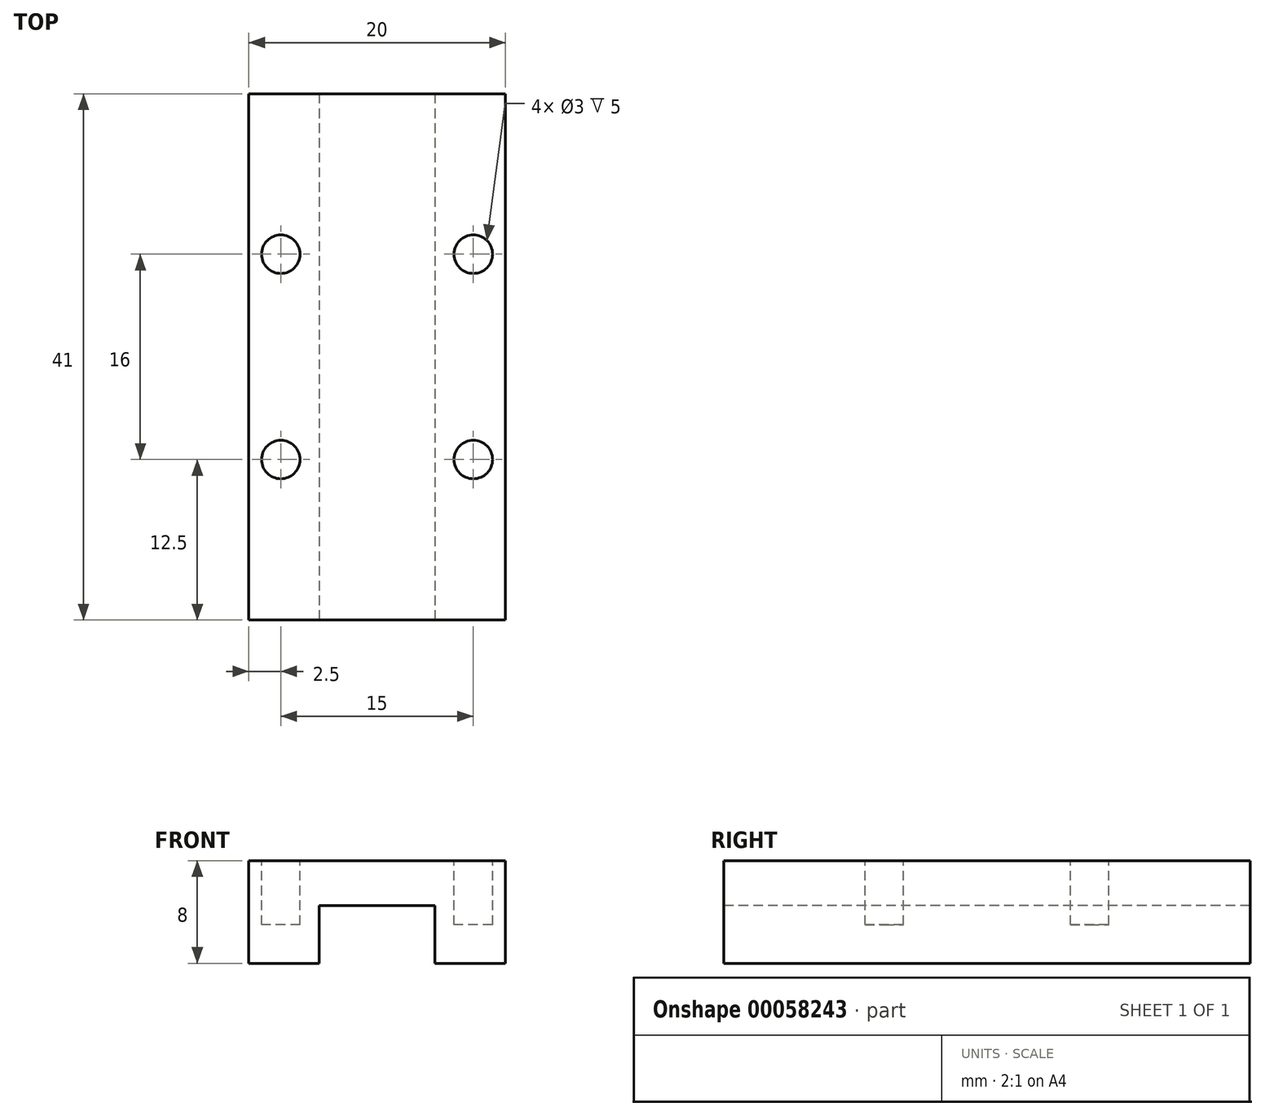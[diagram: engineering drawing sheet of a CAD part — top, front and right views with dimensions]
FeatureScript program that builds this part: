
annotation { "Feature Type Name" : "Feature", "Feature Type Description" : "" }
export const myFeature = defineFeature(function(context is Context, id is Id, definition is map)
    precondition{}
    {
        {
            var Q0;
            Q0=qCreatedBy(makeId("Front.planeOp"),FACE);
            var sketch = newSketch(context, id + "F0", { "sketchPlane" : qUnion([Q0])});
            skLineSegment(sketch, "E0", {"start": v(0, 0) * mm, "end": v(0, 12.26) * mm, "construction": true});
            skLineSegment(sketch, "E1.rect.bottom", {"start": v(10, 4) * mm, "end": v(-10, 4) * mm});
            skLineSegment(sketch, "E1.rect.top", {"start": v(10, -4) * mm, "end": v(-10, -4) * mm});
            skLineSegment(sketch, "E1.rect.left", {"start": v(10, 4) * mm, "end": v(10, -4) * mm});
            skLineSegment(sketch, "E1.rect.right", {"start": v(-10, 4) * mm, "end": v(-10, -4) * mm});
            skPoint(sketch, "E1.rect.middle", {"position": v(0, 0) * mm});
            skSolve(sketch);
        }
        {
            var Q0;
            Q0 = qSketchRegion(id + "F0", true);
            extrude(context, id + "F1", {"entities" : qUnion([Q0]), "depth" : 41 * mm, "symmetric" : true});
        }
        {
            var Q0;
            Q0=makeQuery(id+"F1.opExtrude","CAP_FACE",FACE,{"disambiguationData":[OSD([sQuery(id+"F0.wireOp",EDGE,"E1.rect.bottom"),sQuery(id+"F0.wireOp",EDGE,"E1.rect.top"),sQuery(id+"F0.wireOp",EDGE,"E1.rect.left"),sQuery(id+"F0.wireOp",EDGE,"E1.rect.right")])],"isStart":false});
            var sketch = newSketch(context, id + "F2", { "sketchPlane" : qUnion([Q0])});
            skLineSegment(sketch, "E2", {"start": v(0, 4) * mm, "end": v(0, -4) * mm, "construction": true});
            skLineSegment(sketch, "E3.bottom", {"start": v(-4.5, -4) * mm, "end": v(4.5, -4) * mm});
            skLineSegment(sketch, "E3.top", {"start": v(-4.5, 0.5) * mm, "end": v(4.5, 0.5) * mm});
            skLineSegment(sketch, "E3.left", {"start": v(-4.5, -4) * mm, "end": v(-4.5, 0.5) * mm});
            skLineSegment(sketch, "E3.right", {"start": v(4.5, -4) * mm, "end": v(4.5, 0.5) * mm});
            skSolve(sketch);
        }
        {
            var Q0;
            Q0 = qSketchRegion(id + "F2", true);
            extrude(context, id + "F3", {"entities" : qUnion([Q0]), "operationType" : NewBodyOperationType.REMOVE, "endBound" : BoundingType.THROUGH_ALL, "oppositeDirection" : true, "depth" : 25 * mm});
        }
        {
            var Q0;
            Q0=makeQuery(id+"F1.opExtrude","SWEPT_FACE",FACE,{"disambiguationData":[OSD([sQuery(id+"F0.wireOp",EDGE,"E1.rect.bottom")])]});
            var sketch = newSketch(context, id + "F4", { "sketchPlane" : qUnion([Q0])});
            skLineSegment(sketch, "E4", {"start": v(0, 20.5) * mm, "end": v(0, 0) * mm, "construction": true});
            skLineSegment(sketch, "E5", {"start": v(0, 0) * mm, "end": v(-10, 0) * mm, "construction": true});
            skCircle(sketch, "E6", {"center": v(-7.5, 8) * mm, "radius": 1.5 * mm});
            skCircle(sketch, "E7.MirrorC", {"center": v(7.5, 8) * mm, "radius": 1.5 * mm});
            skCircle(sketch, "E8.MirrorC", {"center": v(7.5, -8) * mm, "radius": 1.5 * mm});
            skCircle(sketch, "E9.MirrorC", {"center": v(-7.5, -8) * mm, "radius": 1.5 * mm});
            skSolve(sketch);
        }
        {
            var Q0;
            Q0 = qSketchRegion(id + "F4", true);
            extrude(context, id + "F5", {"entities" : qUnion([Q0]), "operationType" : NewBodyOperationType.REMOVE, "oppositeDirection" : true, "depth" : 5 * mm});
        }
    });
